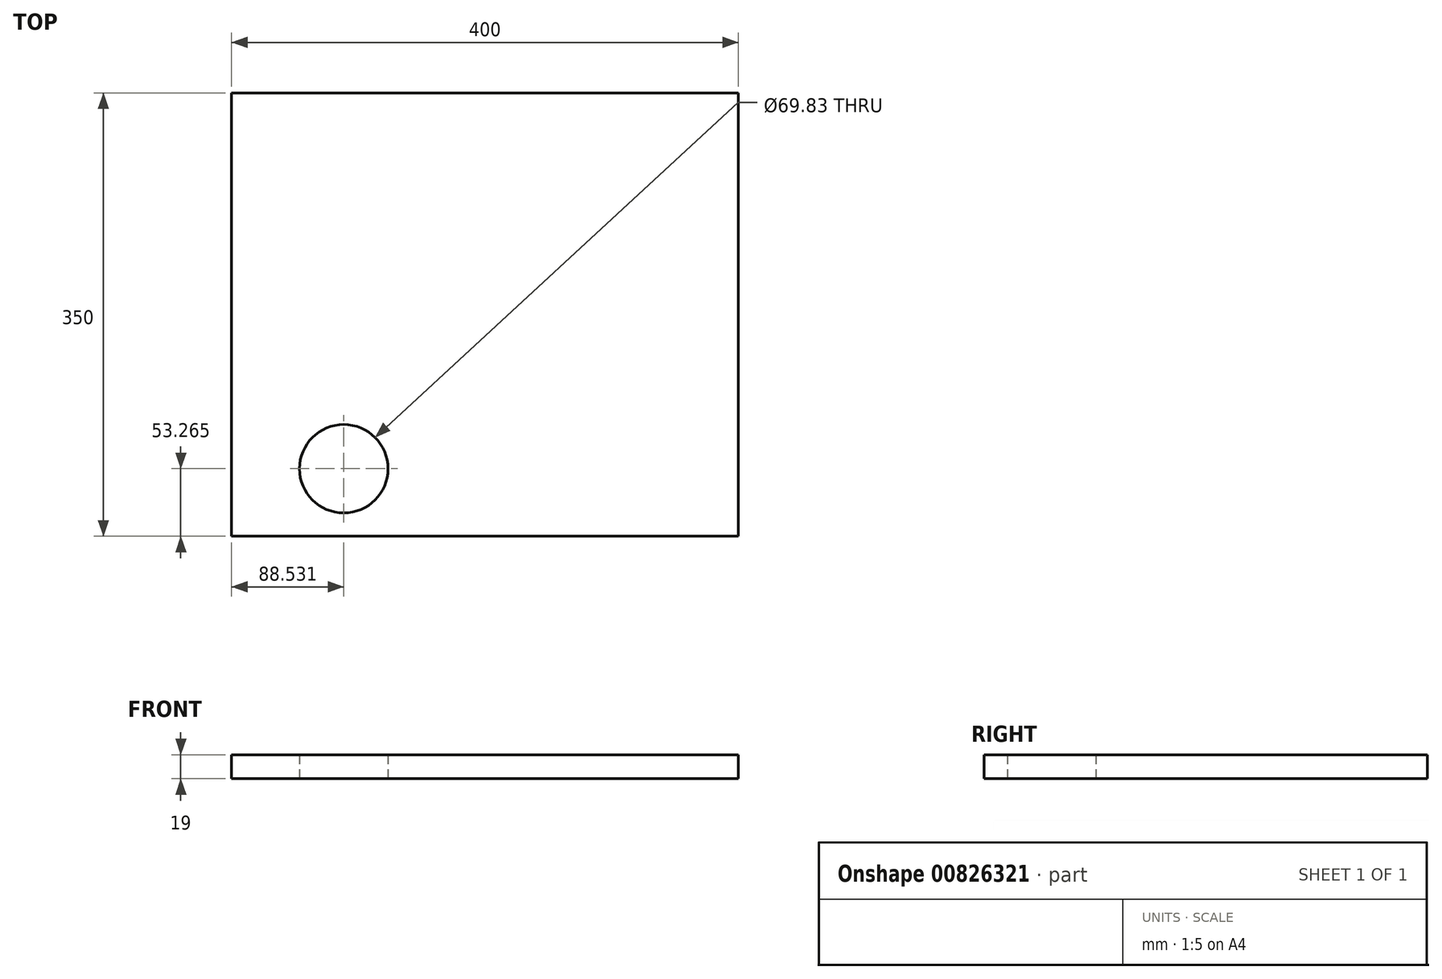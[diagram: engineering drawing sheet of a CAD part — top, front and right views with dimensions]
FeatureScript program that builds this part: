
annotation { "Feature Type Name" : "Feature", "Feature Type Description" : "" }
export const myFeature = defineFeature(function(context is Context, id is Id, definition is map)
    precondition{}
    {
        {
            var Q0;
            Q0=qCreatedBy(makeId("Top.planeOp"),FACE);
            var sketch = newSketch(context, id + "F0", { "sketchPlane" : qUnion([Q0])});
            skLineSegment(sketch, "E0.bottom", {"start": v(200, 175) * mm, "end": v(-200, 175) * mm});
            skLineSegment(sketch, "E0.top", {"start": v(200, -175) * mm, "end": v(-200, -175) * mm});
            skLineSegment(sketch, "E0.left", {"start": v(200, 175) * mm, "end": v(200, -175) * mm});
            skLineSegment(sketch, "E0.right", {"start": v(-200, 175) * mm, "end": v(-200, -175) * mm});
            skPoint(sketch, "E0.middle", {"position": v(0, 0) * mm});
            skCircle(sketch, "E1", {"center": v(-111.47, -121.74) * mm, "radius": 34.91 * mm});
            skPoint(sketch, "E1.first.point", {"position": v(-139.44, -100.85) * mm});
            skPoint(sketch, "E1.second.point", {"position": v(-119.33, -155.75) * mm});
            skPoint(sketch, "E1.third.point", {"position": v(-78.56, -110.09) * mm});
            skFitSpline(sketch, "E2", {"points": [v(200, -116.7) * mm, v(182.4, -157.93) * mm, v(130.17, -175) * mm], "startDerivative": vector(0, -57.4) * mm, "endDerivative": vector(-82.84, 0) * mm});
            skFitSpline(sketch, "E3", {"points": [v(-147.6, -175) * mm, v(-185.65, -159.56) * mm, v(-200, -122.6) * mm], "startDerivative": vector(-61.57, 5.24) * mm, "endDerivative": vector(-10.97, 64.37) * mm});
            skFitSpline(sketch, "E4", {"points": [v(-200, 108.93) * mm, v(-183.48, 157.93) * mm, v(-137.75, 175) * mm], "startDerivative": vector(0, 109.6) * mm, "endDerivative": vector(115.92, 0) * mm});
            skFitSpline(sketch, "E5", {"points": [v(141.38, 175) * mm, v(183.48, 161.73) * mm, v(200, 110.97) * mm], "startDerivative": vector(97.54, 0) * mm, "endDerivative": vector(0, -109.84) * mm});
            skSolve(sketch);
        }
        {
            var Q0;
            Q0 = qSketchRegion(id + "F0", true);
            extrude(context, id + "F1", {"entities" : qUnion([Q0]), "depth" : 19 * mm, "offsetDistance" : 25 * mm});
        }
        {
            var Q0;
            Q0=makeQuery(id+"F0.imprint","IMPRINT",FACE,{"disambiguationData":[TD([[makeQuery(id+"F0.imprint","IMPRINT",EDGE,{"derivedFrom":sQuery(id+"F0.wireOp",EDGE,"E1")}),1.0]])]});
            extrude(context, id + "F2", {"entities" : qUnion([Q0]), "operationType" : NewBodyOperationType.REMOVE, "endBound" : BoundingType.THROUGH_ALL, "oppositeDirection" : true, "depth" : 25 * mm, "offsetDistance" : 25 * mm});
        }
        {
            var Q0;
            {var subQ3=sQuery(id+"F0.wireOp",EDGE,"E3");Q0=makeQuery(id+"F0.imprint","IMPRINT",FACE,{"disambiguationData":[TD([[makeQuery(id+"F0.imprint","IMPRINT",EDGE,{"derivedFrom":subQ3}),1.0]])]});}
            extrude(context, id + "F3", {"entities" : qUnion([Q0]), "operationType" : NewBodyOperationType.REMOVE, "endBound" : BoundingType.THROUGH_ALL, "oppositeDirection" : true, "depth" : 25 * mm, "offsetDistance" : 25 * mm});
        }
    });
